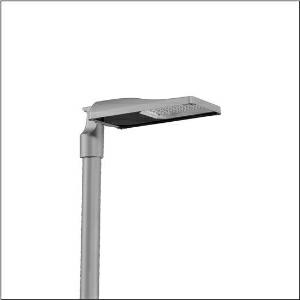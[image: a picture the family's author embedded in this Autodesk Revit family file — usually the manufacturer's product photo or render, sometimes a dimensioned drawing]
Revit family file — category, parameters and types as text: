
# Revit family: streetlight_sl_31_mini___st1_0a_5xh6d31a08ga_ae29
name_source: partatom
category: Lighting Fixtures
units: mm (PartAtom-declared; Revit-internal decimal feet)

## family parameters
Cut with Voids When Loaded = No
Host = Face
Light Source = No
Part Type = Normal
Room Calculation Point = No
Round Connector Dimension = Use Diameter
Shared = No

## types (1)
- --- (1 x LED, 5710 lm, 37.3 W, 3000K)
    Apparent Load = 37 VA
    CIE Flux Codes = 37 72 97 100 100
    Color Rendering = 70
    Color Temperature = 3000K
    Default Elevation = 1800 mm
    Description = Streetlight SL 31 mini Easy, Desk-Remote mast luminaire for post-top, side-entry; light control with lens of PMMA; light distribution: ST1.0a, direct asymmetric distribution, for standard-compliant lighting for roads and squares; LED: luminous flux: 5.710lm, light colour: 730, colour temperature: 3000K; luminous efficacy: 153,1lm/W; control: pre-setting: linear dimming characteristic, flexible luminous flux parameterisation, time-dependent luminous flux control, constant luminous flux control, intelligent temperature release in ECG and LED module, overheat protection; luminaire housing, of diecast aluminium, SITECO metallic grey (DB 702S), corrosivity category C5 high according to DIN EN ISO 12944; cover of toughened safety glass, transparent, opened without tools; mast flange of diecast aluminium, SITECO metallic grey (DB 702S), spigot size: 76/60mm, mast flange included unmounted; with cable H07RN-F 2x 1.5mm², cable length: 6,5m, connection cable pre-assembled; mains connection: 220..240V, AC, 50/60Hz; power consumption (at start of service life): 37,3W / (at end of service life): 38,7W / (with reduced operation 50%): 17,5W; protection rating (complete): IP66; insulation class (complete): insulation class II (safety insulation); impact resistance: IK10; certification: CE, ENEC, ENEC+, VDE, UKCA; permissible operating ambient temperature for outdoor applications: -40..+50°C; packaging unit: 1 piece

Light Distribution: ST1.0a
    Height = 76 mm
    Lamp = 1 x LED
    Lamp Light Flux = 5710 lm
    Lamp Power = 37.3 W
    Lamp count = 1
    Length = 547 mm
    Luminous efficacy = 153 lm/W
    Manufacturer = Siteco
    ModVariant = No
    Model = 5XH6D31A08GA
    Number of Poles = 1
    OnlyDefault = Yes
    Power Factor = 1
    Product Name = Streetlight SL 31 mini | ST1.0a
    Product group = mast luminaire | pylon top
    ProductGroupID = 6100
    Protection Class = Protection class II
    Protection Degree = IP 66
    RLX_Detail_Level = 1
    RLX_Emergency_Light_Flux = 0 lm
    RLX_Emergency_Type = 0
    RLX_Emergency_Type_DB = No
    RlxData = <blob elided: 39665 chars, md5=a1f83fe0>
    Socket = socket
    Standby Power = 0 W
    System Light Flux = 5710 lm
    System Power = 37 W
    Type Comments = factory setting: luminous flux: 100 % | dim-lin: 254 | 386 mA
    Type Image = l_1300326.jpg
    URL = http://relux.com
    VarID = @adj_061097
    Voltage = 0 V
    Weight = 0.00 kg
    Width = 265 mm

## geometry (parser evidence)
native form markers: Blend x4, Sweep x8
no freeform markers — native parametric forms only
